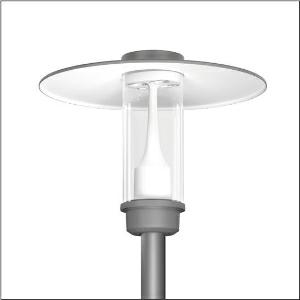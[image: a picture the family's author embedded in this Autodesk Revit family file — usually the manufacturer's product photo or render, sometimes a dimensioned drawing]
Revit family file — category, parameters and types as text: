
# Revit family: litepole_2_iq___p1_0a_5xa5425nf14h_2791
name_source: partatom
category: Lighting Fixtures
units: mm (PartAtom-declared; Revit-internal decimal feet)

## family parameters
Cut with Voids When Loaded = No
Host = Face
Light Source = No
Part Type = Normal
Room Calculation Point = No
Round Connector Dimension = Use Diameter
Shared = No

## types (1)
- --- (1 x LED, 1520 lm, 11.8 W, 2700K)
    Apparent Load = 12 VA
    CIE Flux Codes = 33 62 89 96 100
    Color Rendering = 70
    Color Temperature = 2700K
    Default Elevation = 1800 mm
    Description = Litepole 2 iQ, mast luminaire, Module 540 iQ-SR, primary light control with 3 zone facetted reflector, of plastic, silver coated, highly specular, structured, primary optical cover: cover, of PMMA, transparent, light distribution: P1.0a, light emission: direct distribution, primary light characteristic: strongly asymmetric, installation type: post-top, LED, High Power LED, rated luminous flux: 1.520lm, luminous efficacy: 129lm/W, light colour: 727, colour temperature: 2700K, control gear: ECG iQ, control: presetting dimming logarithmic, Street-Remote, Auto-Match, Temp-Guard, Lumen-Switch, Night-Set, Smart-Wire, Light-Fading, Desk-Remote (wireless, voltage-free reading and setting of iQ features in the workshop via application-optimized NFC function/RFID function), optimised constant luminous flux control (CLO 2.0), with terminal, 6-pole, max. 2.5mm², mains connection: 230..240V, AC, 50/60Hz, start of lifetime: 12W, end of service life: 12W, reduction: 6W, luminaire housing, upper part, of aluminium, coated, Siteco® metallic grey (DB 702S), diameter: 750mm, height: 590mm, spigot size: d x l = 76 x 70mm (post-top) | with reducer (optional accessory) 60 x 70mm, post-top mast mounting element, of diecast aluminium, coated, Siteco® metallic grey (DB 702S), Module 540 iQ-SR, traffic white (RAL 9016), equipment: standard, protection rating (complete): IP65, insulation class (complete): insulation class II (safety insulation), certification: CE, ENEC, VDE, packaging unit: 1 piece

Light Distribution: P1.0a
    Height = 590 mm
    Lamp = 1 x LED
    Lamp Light Flux = 1520 lm
    Lamp Power = 11.8 W
    Lamp count = 1
    Length = 750 mm
    Luminous efficacy = 129 lm/W
    Manufacturer = Siteco
    ModVariant = No
    Model = 5XA5425NF14H
    Number of Poles = 1
    OnlyDefault = Yes
    Power Factor = 1
    Product Name = Litepole 2 iQ | P1.0a
    Product group = mast luminaire | pylon top
    ProductGroupID = 6100
    Protection Class = Protection class II
    Protection Degree = IP 65
    RLX_Detail_Level = 1
    RLX_Emergency_Light_Flux = 0 lm
    RLX_Emergency_Type = 0
    RLX_Emergency_Type_DB = No
    RlxData = <blob elided: 138493 chars, md5=00045940>
    Socket = socket
    Standby Power = 0 W
    System Light Flux = 1520 lm
    System Power = 12 W
    Type Comments = factory setting: luminous flux: 100 % | dim-lin: 254 | 472 mA
    Type Image = l_1006518.jpg
    URL = http://relux.com
    VarID = @adj_084705
    Voltage = 0 V
    Weight = 0.00 kg
    Width = 0 mm  [stored 0 ft]

note: [stored X ft] marks values corroborated as IEEE doubles in the binary element streams (Revit-internal decimal feet)

## geometry (parser evidence)
native form markers: Blend x4, Sweep x7
no freeform markers — native parametric forms only
